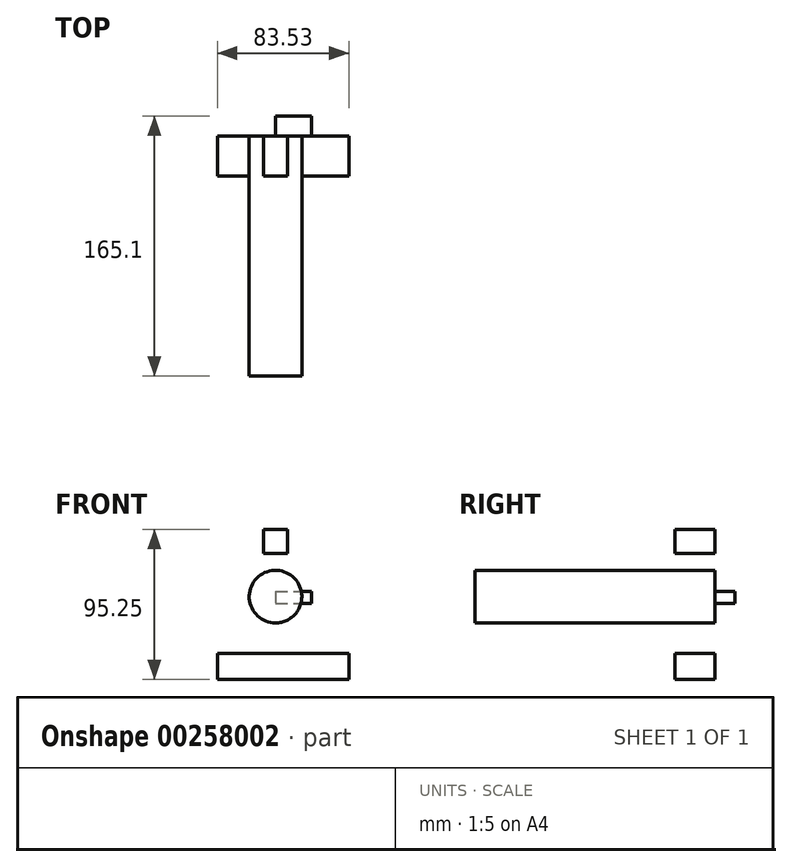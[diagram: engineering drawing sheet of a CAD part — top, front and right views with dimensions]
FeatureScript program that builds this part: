
annotation { "Feature Type Name" : "Feature", "Feature Type Description" : "" }
export const myFeature = defineFeature(function(context is Context, id is Id, definition is map)
    precondition{}
    {
        {
            var Q0;
            Q0=qCreatedBy(makeId("Front.planeOp"),FACE);
            var sketch = newSketch(context, id + "F0", { "sketchPlane" : qUnion([Q0])});
            skCircle(sketch, "E0", {"center": v(0, 0) * mm, "radius": 16.7 * mm});
            skLineSegment(sketch, "E1.bottom", {"start": v(-7.62, 42.64) * mm, "end": v(7.62, 42.64) * mm});
            skLineSegment(sketch, "E1.top", {"start": v(-7.62, 27.4) * mm, "end": v(7.62, 27.4) * mm});
            skLineSegment(sketch, "E1.left", {"start": v(-7.62, 42.64) * mm, "end": v(-7.62, 27.4) * mm});
            skLineSegment(sketch, "E1.right", {"start": v(7.62, 42.64) * mm, "end": v(7.62, 27.4) * mm});
            skPoint(sketch, "E1.middle", {"position": v(0, 35.02) * mm});
            skLineSegment(sketch, "E2.bottom", {"start": v(-36.93, -36.2) * mm, "end": v(46.6, -36.2) * mm});
            skLineSegment(sketch, "E2.top", {"start": v(-36.93, -52.6) * mm, "end": v(46.6, -52.6) * mm});
            skLineSegment(sketch, "E2.left", {"start": v(-36.93, -36.2) * mm, "end": v(-36.93, -52.6) * mm});
            skLineSegment(sketch, "E2.right", {"start": v(46.6, -36.2) * mm, "end": v(46.6, -52.6) * mm});
            skSolve(sketch);
        }
        {
            var Q0;
            Q0=makeQuery(id+"F0.imprint","IMPRINT",FACE,{"disambiguationData":[TD([[makeQuery(id+"F0.imprint","IMPRINT",EDGE,{"derivedFrom":sQuery(id+"F0.wireOp",EDGE,"E0")}),1.0]])]});
            extrude(context, id + "F1", {"entities" : qUnion([Q0]), "depth" : 127 * mm});
        }
        {
            var Q0;
            Q0=makeQuery(id+"F0.imprint","IMPRINT",FACE,{"disambiguationData":[TD([[makeQuery(id+"F0.imprint","IMPRINT",EDGE,{"derivedFrom":sQuery(id+"F0.wireOp",EDGE,"E0")}),1.0]])]});
            var Q1;
            Q1=makeQuery(id+"F0.imprint","IMPRINT",FACE,{"disambiguationData":[TD([[makeQuery(id+"F0.imprint","IMPRINT",EDGE,{"derivedFrom":sQuery(id+"F0.wireOp",EDGE,"E2.bottom")}),-1.0]])]});
            var Q2;
            Q2=makeQuery(id+"F0.imprint","IMPRINT",FACE,{"disambiguationData":[TD([[makeQuery(id+"F0.imprint","IMPRINT",EDGE,{"derivedFrom":sQuery(id+"F0.wireOp",EDGE,"E1.bottom")}),-1.0]])]});
            var Q3;
            Q3=makeQuery(id+"F1.opExtrude","CAP_FACE",FACE,{"disambiguationData":[OSD([sQuery(id+"F0.wireOp",EDGE,"E0")])],"isStart":false});
            extrude(context, id + "F2", {"entities" : qUnion([Q0, Q1, Q2, Q3]), "operationType" : NewBodyOperationType.ADD, "depth" : 25.4 * mm});
        }
        {
            var Q0;
            Q0=qCreatedBy(makeId("Front.planeOp"),FACE);
            var sketch = newSketch(context, id + "F3", { "sketchPlane" : qUnion([Q0])});
            skLineSegment(sketch, "E3.bottom", {"start": v(0, 3.41) * mm, "end": v(23, 3.41) * mm});
            skLineSegment(sketch, "E3.top", {"start": v(0, -4.2) * mm, "end": v(23, -4.2) * mm});
            skLineSegment(sketch, "E3.left", {"start": v(0, 3.41) * mm, "end": v(0, -4.2) * mm});
            skLineSegment(sketch, "E3.right", {"start": v(23, 3.41) * mm, "end": v(23, -4.2) * mm});
            skSolve(sketch);
        }
        {
            var Q0;
            Q0 = qSketchRegion(id + "F3", true);
            extrude(context, id + "F4", {"entities" : qUnion([Q0]), "operationType" : NewBodyOperationType.ADD, "oppositeDirection" : true, "depth" : 12.7 * mm});
        }
    });
